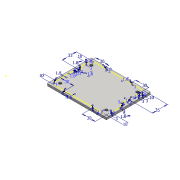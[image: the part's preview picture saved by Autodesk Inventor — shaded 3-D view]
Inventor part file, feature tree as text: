
AUTODESK INVENTOR PART (.ipt)
format: ipt  version: 2016 (Build 200138000, 138)  size: 307,200 bytes
history: native  units: mm
features: extrude x4, sketch x2, other x2, fillet x2, hole x1, pattern_linear x1
ambient origin geometry x8: Origin, YZ Plane, XZ Plane, XY Plane, X Axis, Y Axis, Z Axis, Center Point
bodies: Solid1 (feature_tree)
feature tree (12):
  sketch  "Sketch1"  dims[d9=60.0mm d10=5.0mm]
  hole  "HOLES1"  [1 undecoded]
  other  "OUTLINE1"
  other  "OUTLINE2"
  extrude  "Extrusion2"  Depth=5.0mm TaperAngle=0.0deg
  fillet  "Fillet1"  Radius=0.5mm
  extrude  "Extrusion7"  Depth=10.0mm
  fillet  "Fillet3"  Radius=3.0mm
  extrude  "Extrusion8"  Depth=10.0mm
  extrude  "Extrusion9"  Depth=10.0mm
  pattern_linear  "Rectangular Pattern2"  Spacing1=3.0mm  [1 undecoded]
  sketch  "Sketch8"  dims[d11=5.0mm d14=5.0mm d15=0.0mm d36=0.5mm d44=3.0mm d45=3.0mm d46=3.0mm d47=3.0mm d48=3.0mm d49=3.0mm d50=3.0mm d51=3.0mm d52=10.0mm d53=10.0mm d56=10.0mm d57=10.0mm d58=0.0mm d59=0.5mm d62=5.0mm d63=2.85mm d64=1.0mm d65=60.0mm d67=360.0deg d69=2.3mm d70=0.0mm d71=5.0mm d72=10.0mm d73=0.0mm d74=20.0mm d76=72.0mm d77=20.0mm d79=107.0mm d80=3.0mm d81=30.0mm d82=1.8mm d83=3.0mm d84=30.0mm d85=1.8mm d86=3.0mm d87=3.0mm d88=3.0mm d90=3.0mm d91=3.0mm d92=3.0mm d93=3.0mm d94=3.0mm d95=3.0mm d96=3.0mm d97=1.8mm d98=10.0mm d99=1.8mm d100=10.0mm d101=1.8mm d102=5.0mm d103=1.8mm d104=5.0mm d105=3.0mm d106=1.8mm d107=35.0mm d108=1.8mm d109=5.0mm d110=1.8mm d111=5.0mm d112=1.8mm d113=10.0mm d114=1.8mm d115=30.0mm d116=1.8mm d117=30.0mm d118=1.8mm d119=10.0mm d120=3.0mm d121=1.8mm d122=33.0mm]
note: 2 required parameter values undecoded (feature->parameter linkage not recoverable at this tier; creation-order binding heuristic only, values carry confidence <= 0.55)
